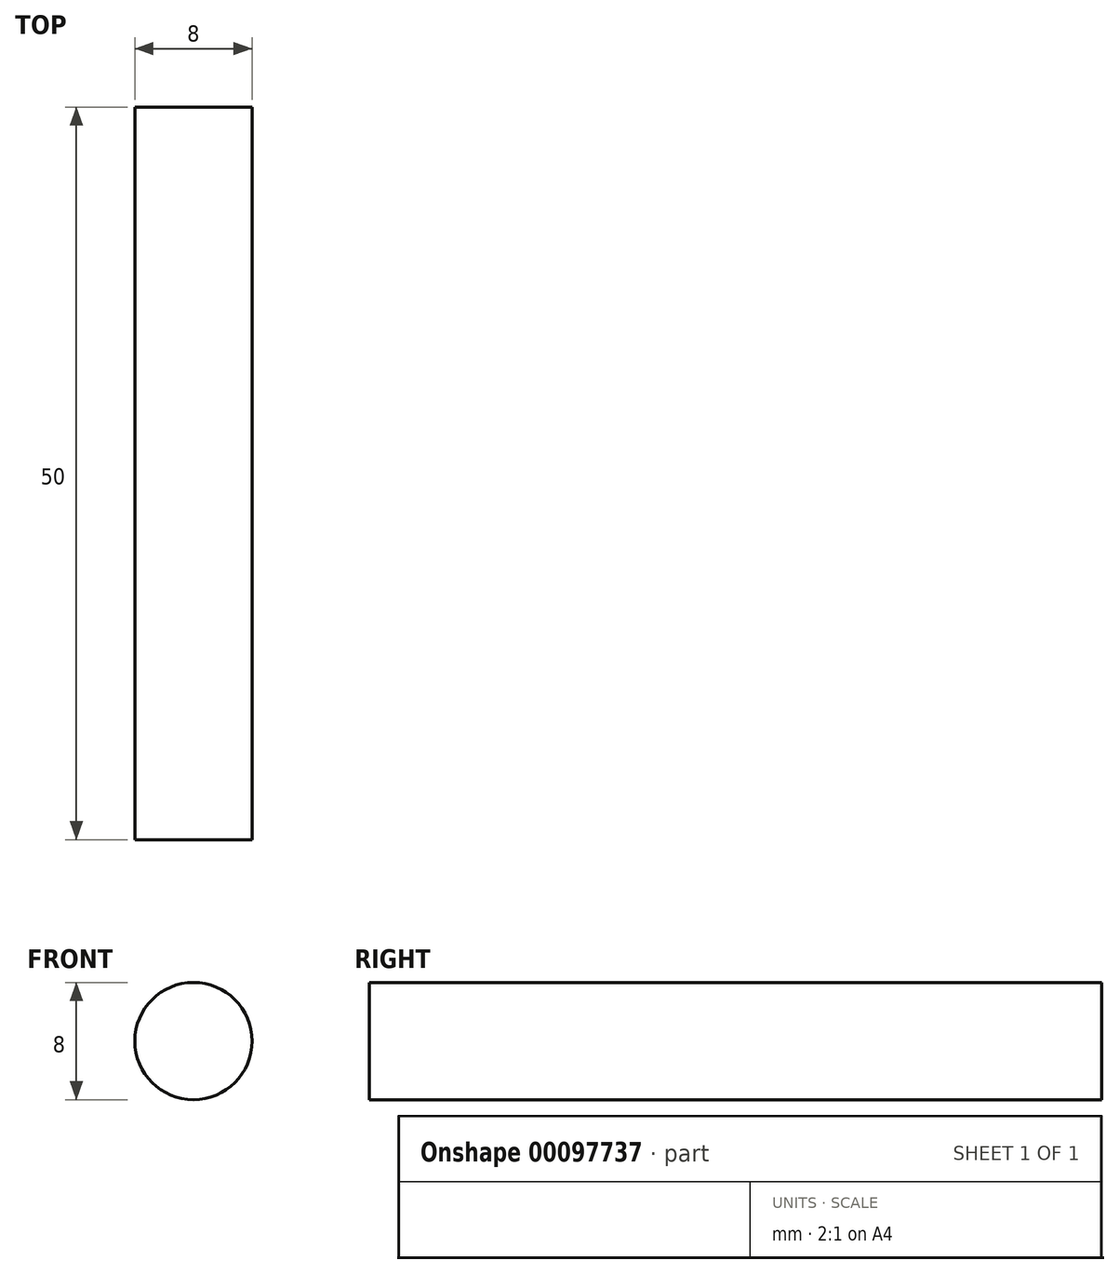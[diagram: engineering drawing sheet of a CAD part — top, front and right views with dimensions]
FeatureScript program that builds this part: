
annotation { "Feature Type Name" : "Feature", "Feature Type Description" : "" }
export const myFeature = defineFeature(function(context is Context, id is Id, definition is map)
    precondition{}
    {
        {
            var Q0;
            Q0=qCreatedBy(makeId("Front.planeOp"),FACE);
            var sketch = newSketch(context, id + "F0", { "sketchPlane" : qUnion([Q0])});
            skCircle(sketch, "E0", {"center": v(0, 0) * mm, "radius": 4 * mm});
            skSolve(sketch);
        }
        {
            var Q0;
            Q0=makeQuery(id+"F0.imprint","IMPRINT",FACE,{"disambiguationData":[TD([[makeQuery(id+"F0.imprint","IMPRINT",EDGE,{"derivedFrom":sQuery(id+"F0.wireOp",EDGE,"E0")}),1.0]])]});
            extrude(context, id + "F1", {"entities" : qUnion([Q0]), "endBound" : BoundingType.SYMMETRIC, "depth" : 50 * mm});
        }
    });
